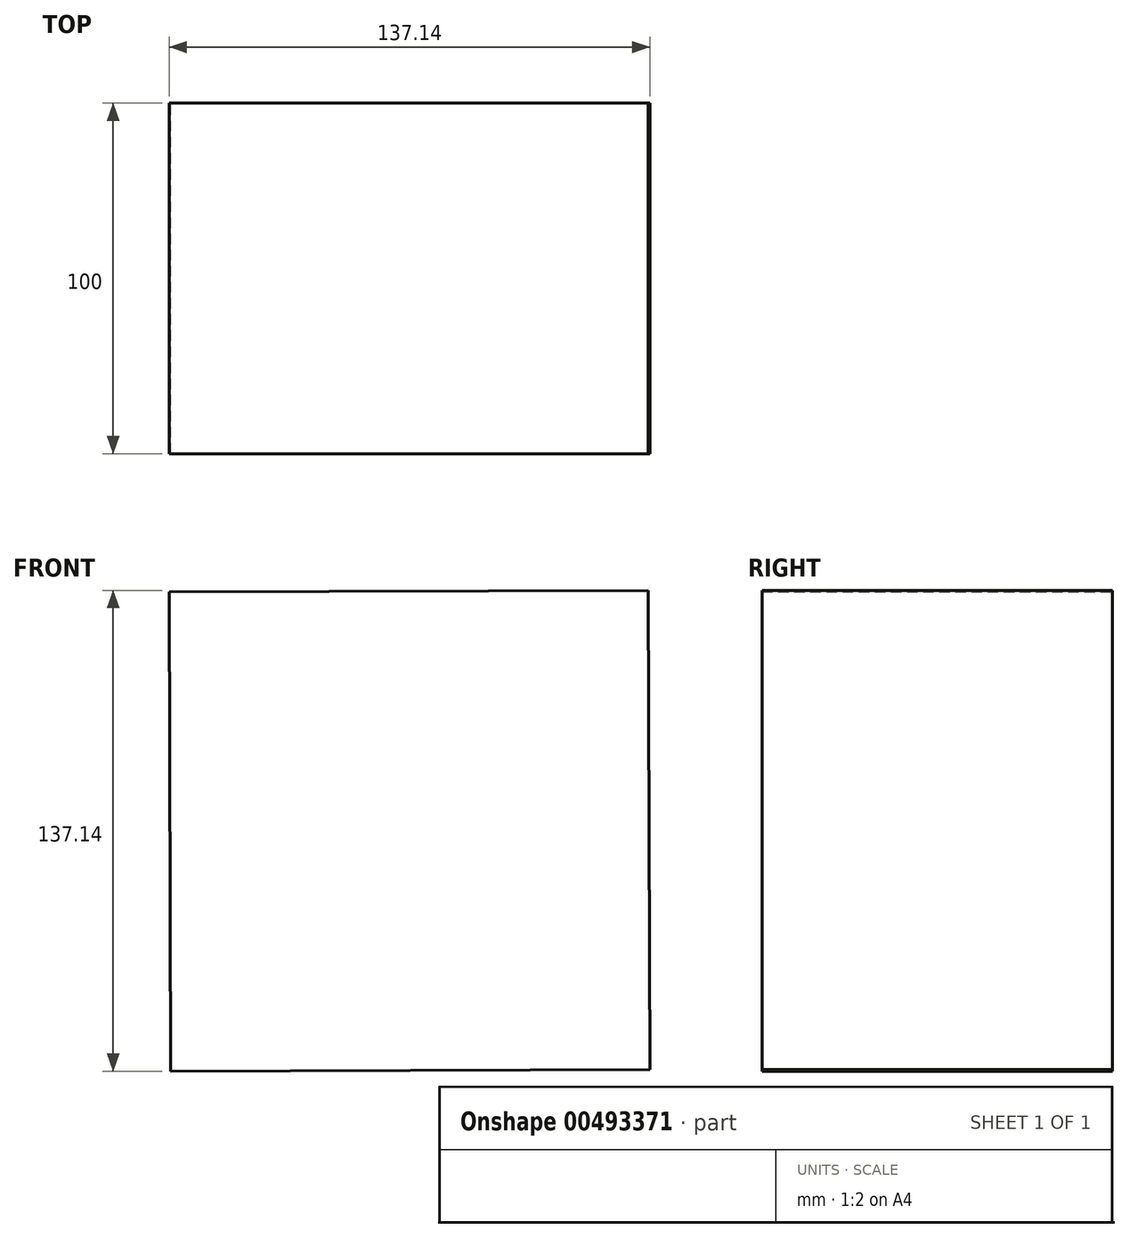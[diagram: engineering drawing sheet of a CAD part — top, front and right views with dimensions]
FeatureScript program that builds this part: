
annotation { "Feature Type Name" : "Feature", "Feature Type Description" : "" }
export const myFeature = defineFeature(function(context is Context, id is Id, definition is map)
    precondition{}
    {
        {
            var Q0;
            Q0=qCreatedBy(makeId("Front.planeOp"),FACE);
            var sketch = newSketch(context, id + "F0", { "sketchPlane" : qUnion([Q0])});
            skCircle(sketch, "E0.cCircle", {"center": v(0, 0) * mm, "radius": 96.66 * mm, "construction": true});
            skLineSegment(sketch, "E0.0", {"start": v(-68.57, 68.14) * mm, "end": v(68.14, 68.57) * mm});
            skLineSegment(sketch, "E0.1", {"start": v(68.14, 68.57) * mm, "end": v(68.57, -68.14) * mm});
            skLineSegment(sketch, "E0.2", {"start": v(68.57, -68.14) * mm, "end": v(-68.14, -68.57) * mm});
            skLineSegment(sketch, "E0.3", {"start": v(-68.14, -68.57) * mm, "end": v(-68.57, 68.14) * mm});
            skSolve(sketch);
        }
        {
            var Q0;
            Q0 = qSketchRegion(id + "F0", true);
            extrude(context, id + "F1", {"entities" : qUnion([Q0]), "endBound" : BoundingType.SYMMETRIC, "depth" : 100 * mm});
        }
    });
